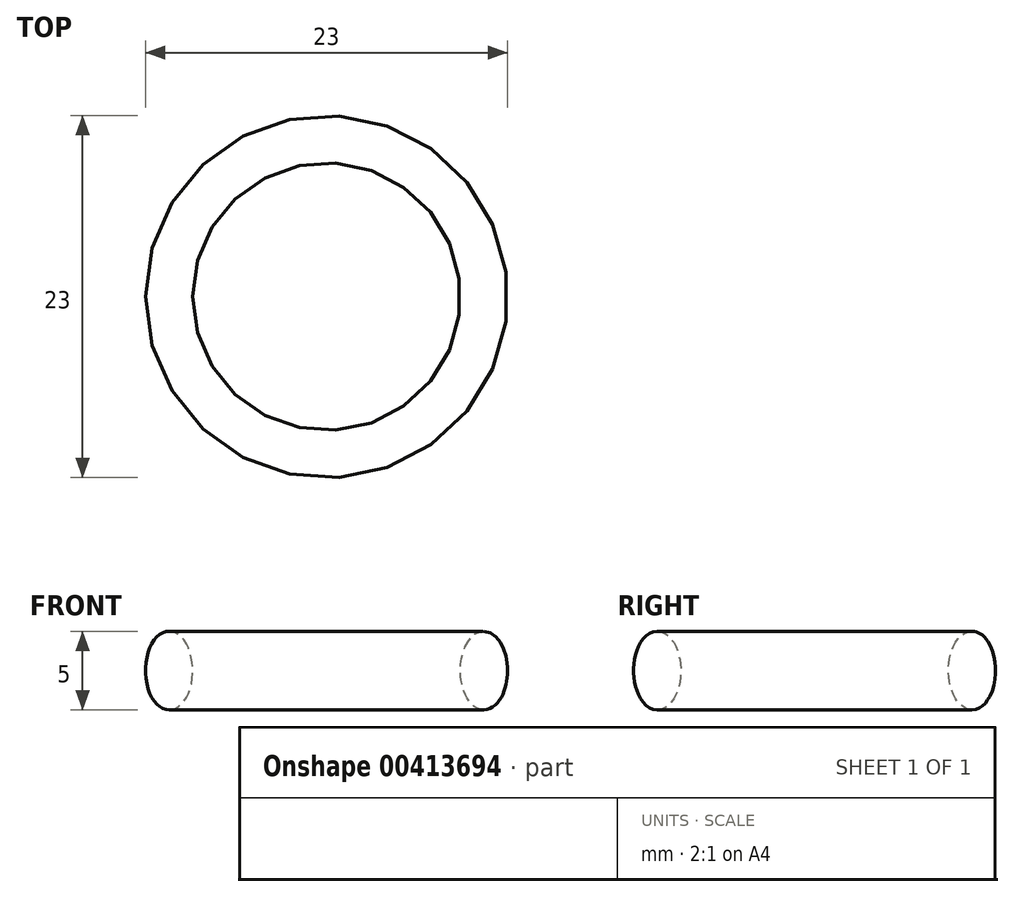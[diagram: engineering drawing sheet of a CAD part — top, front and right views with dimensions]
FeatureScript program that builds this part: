
annotation { "Feature Type Name" : "Feature", "Feature Type Description" : "" }
export const myFeature = defineFeature(function(context is Context, id is Id, definition is map)
    precondition{}
    {
        {
            var Q0;
            Q0=qCreatedBy(makeId("Front.planeOp"),FACE);
            var sketch = newSketch(context, id + "F0", { "sketchPlane" : qUnion([Q0])});
            skEllipse(sketch, "E0", {"center": v(-10, 0) * mm, "majorRadius": 2.5 * mm, "minorRadius": 1.5 * mm, "majorAxis": v(0, 1)});
            skLineSegment(sketch, "E1", {"start": v(0, -7.9) * mm, "end": v(0, 52.44) * mm});
            skSolve(sketch);
        }
        {
            var Q0;
            Q0=makeQuery(id+"F0.imprint","IMPRINT",FACE,{"disambiguationData":[TD([[makeQuery(id+"F0.imprint","IMPRINT",EDGE,{"derivedFrom":sQuery(id+"F0.wireOp",EDGE,"E0")}),1.0]])]});
            var Q1;
            Q1=sQuery(id+"F0.wireOp",EDGE,"E1");
            revolve(context, id + "F1", {"entities" : qUnion([Q0]), "axis" : qUnion([Q1]), "revolveType" : RevolveType.FULL});
        }
    });
